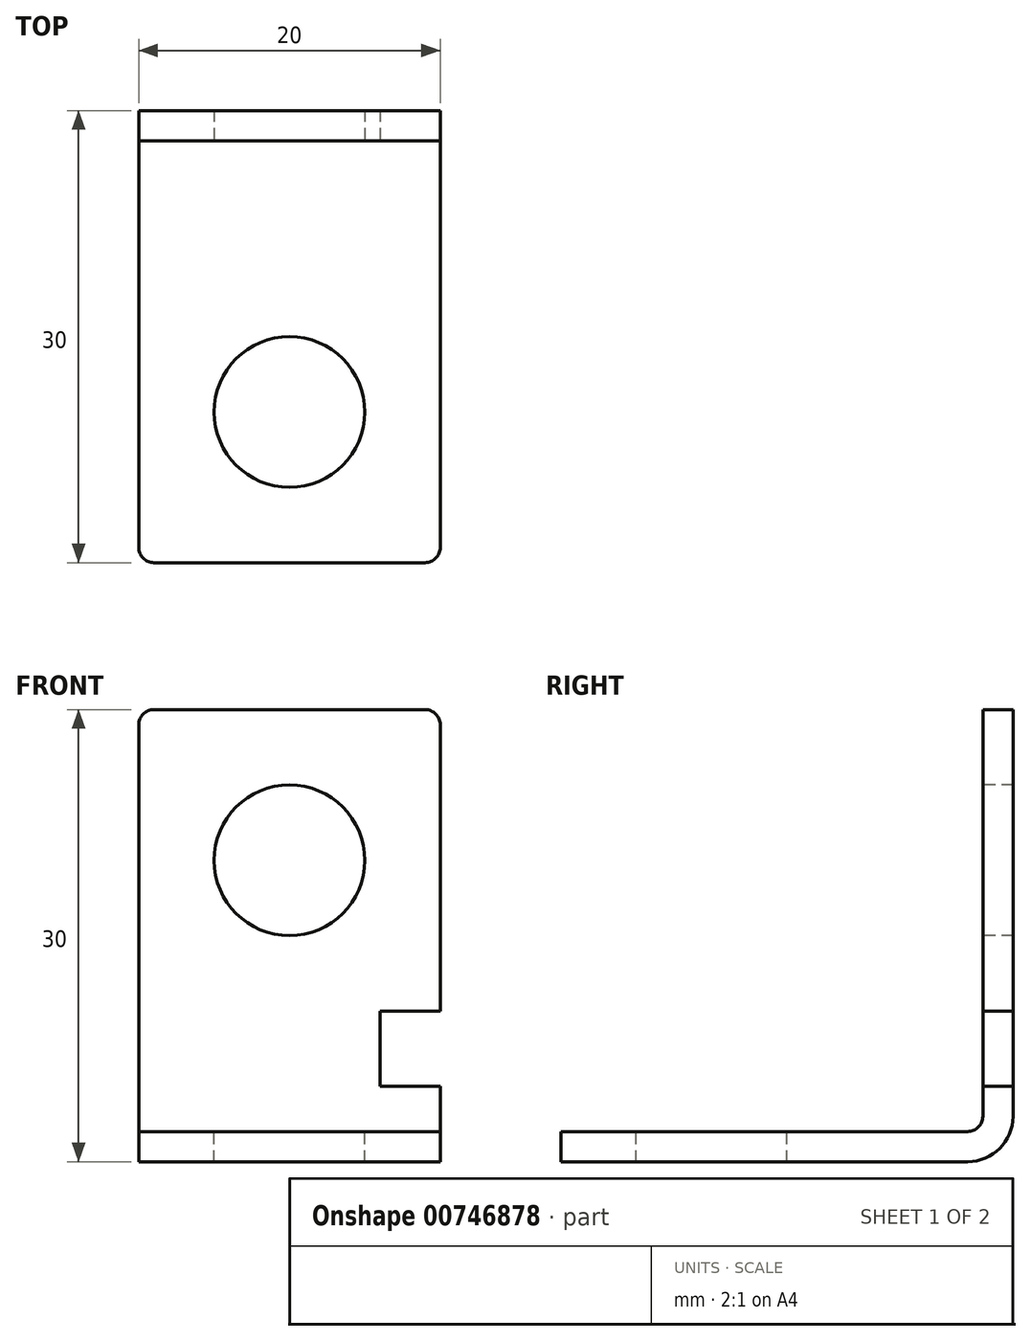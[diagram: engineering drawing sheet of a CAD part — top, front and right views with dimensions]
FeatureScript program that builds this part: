
annotation { "Feature Type Name" : "Feature", "Feature Type Description" : "" }
export const myFeature = defineFeature(function(context is Context, id is Id, definition is map)
    precondition{}
    {
        {
            var Q0;
            Q0=qCreatedBy(makeId("Right.planeOp"),FACE);
            var sketch = newSketch(context, id + "F0", { "sketchPlane" : qUnion([Q0])});
            skLineSegment(sketch, "E0.bottom", {"start": v(0, 0) * mm, "end": v(27, 0) * mm});
            skLineSegment(sketch, "E0.left", {"start": v(0, 0) * mm, "end": v(0, 2) * mm});
            skLineSegment(sketch, "E0.right", {"start": v(30, 3) * mm, "end": v(30, 30) * mm});
            skLineSegment(sketch, "E1", {"start": v(0, 2) * mm, "end": v(27, 2) * mm});
            skLineSegment(sketch, "E2", {"start": v(28, 3) * mm, "end": v(28, 30) * mm});
            skLineSegment(sketch, "E3", {"start": v(28, 30) * mm, "end": v(30, 30) * mm});
            skPoint(sketch, "E4.visualSharp", {"position": v(30, 0) * mm});
            skArc(sketch, "E4.filletArc", {"start": v(27, 0) * mm, "mid": v(29.12, 0.88) * mm, "end": v(30, 3) * mm});
            skPoint(sketch, "E5.visualSharp", {"position": v(28, 2) * mm});
            skArc(sketch, "E6", {"start": v(27, 2) * mm, "mid": v(27.7, 2.3) * mm, "end": v(28, 3) * mm});
            skSolve(sketch);
        }
        {
            var Q0;
            Q0 = qSketchRegion(id + "F0", true);
            extrude(context, id + "F1", {"entities" : qUnion([Q0]), "oppositeDirection" : true, "depth" : 20 * mm, "offsetDistance" : 25 * mm});
        }
        {
            var Q0;
            Q0=makeQuery(id+"F1.opExtrude","SWEPT_FACE",FACE,{"disambiguationData":[OSD([sQuery(id+"F0.wireOp",EDGE,"E2")])]});
            var sketch = newSketch(context, id + "F2", { "sketchPlane" : qUnion([Q0])});
            skCircle(sketch, "E7", {"center": v(-10, 20) * mm, "radius": 5 * mm});
            skLineSegment(sketch, "E8.bottom", {"start": v(0, 10) * mm, "end": v(-4, 10) * mm});
            skLineSegment(sketch, "E8.top", {"start": v(0, 5) * mm, "end": v(-4, 5) * mm});
            skLineSegment(sketch, "E8.left", {"start": v(0, 10) * mm, "end": v(0, 5) * mm});
            skLineSegment(sketch, "E8.right", {"start": v(-4, 10) * mm, "end": v(-4, 5) * mm});
            skSolve(sketch);
        }
        {
            var Q0;
            Q0 = qSketchRegion(id + "F2", true);
            extrude(context, id + "F3", {"entities" : qUnion([Q0]), "operationType" : NewBodyOperationType.REMOVE, "endBound" : BoundingType.THROUGH_ALL, "oppositeDirection" : true, "depth" : 25 * mm, "offsetDistance" : 25 * mm});
        }
        {
            var Q0;
            Q0=makeQuery(id+"F1.opExtrude","SWEPT_FACE",FACE,{"disambiguationData":[OSD([sQuery(id+"F0.wireOp",EDGE,"E1")])]});
            var sketch = newSketch(context, id + "F4", { "sketchPlane" : qUnion([Q0])});
            skCircle(sketch, "E9", {"center": v(-10, 10) * mm, "radius": 5 * mm});
            skSolve(sketch);
        }
        {
            var Q0;
            Q0 = qSketchRegion(id + "F4", true);
            extrude(context, id + "F5", {"entities" : qUnion([Q0]), "operationType" : NewBodyOperationType.REMOVE, "endBound" : BoundingType.THROUGH_ALL, "oppositeDirection" : true, "depth" : 25 * mm, "offsetDistance" : 25 * mm});
        }
        {
            var Q0;
            Q0=makeQuery(id+"F1.opExtrude","CAP_EDGE",EDGE,{"disambiguationData":[OSD([sQuery(id+"F0.wireOp",EDGE,"E0.left")])],"isStart":true});
            var Q1;
            Q1=makeQuery(id+"F1.opExtrude","CAP_EDGE",EDGE,{"disambiguationData":[OSD([sQuery(id+"F0.wireOp",EDGE,"E0.left")])],"isStart":false});
            var Q2;
            Q2=makeQuery(id+"F1.opExtrude","CAP_EDGE",EDGE,{"disambiguationData":[OSD([sQuery(id+"F0.wireOp",EDGE,"E3")])],"isStart":true});
            var Q3;
            Q3=makeQuery(id+"F1.opExtrude","CAP_EDGE",EDGE,{"disambiguationData":[OSD([sQuery(id+"F0.wireOp",EDGE,"E3")])],"isStart":false});
            fillet(context, id + "F6", {"entities" : qUnion([Q0, Q1, Q2, Q3]), "radius" : 1 * mm, "tangentPropagation" : true, "allowEdgeOverflow" : false});
        }
    });
